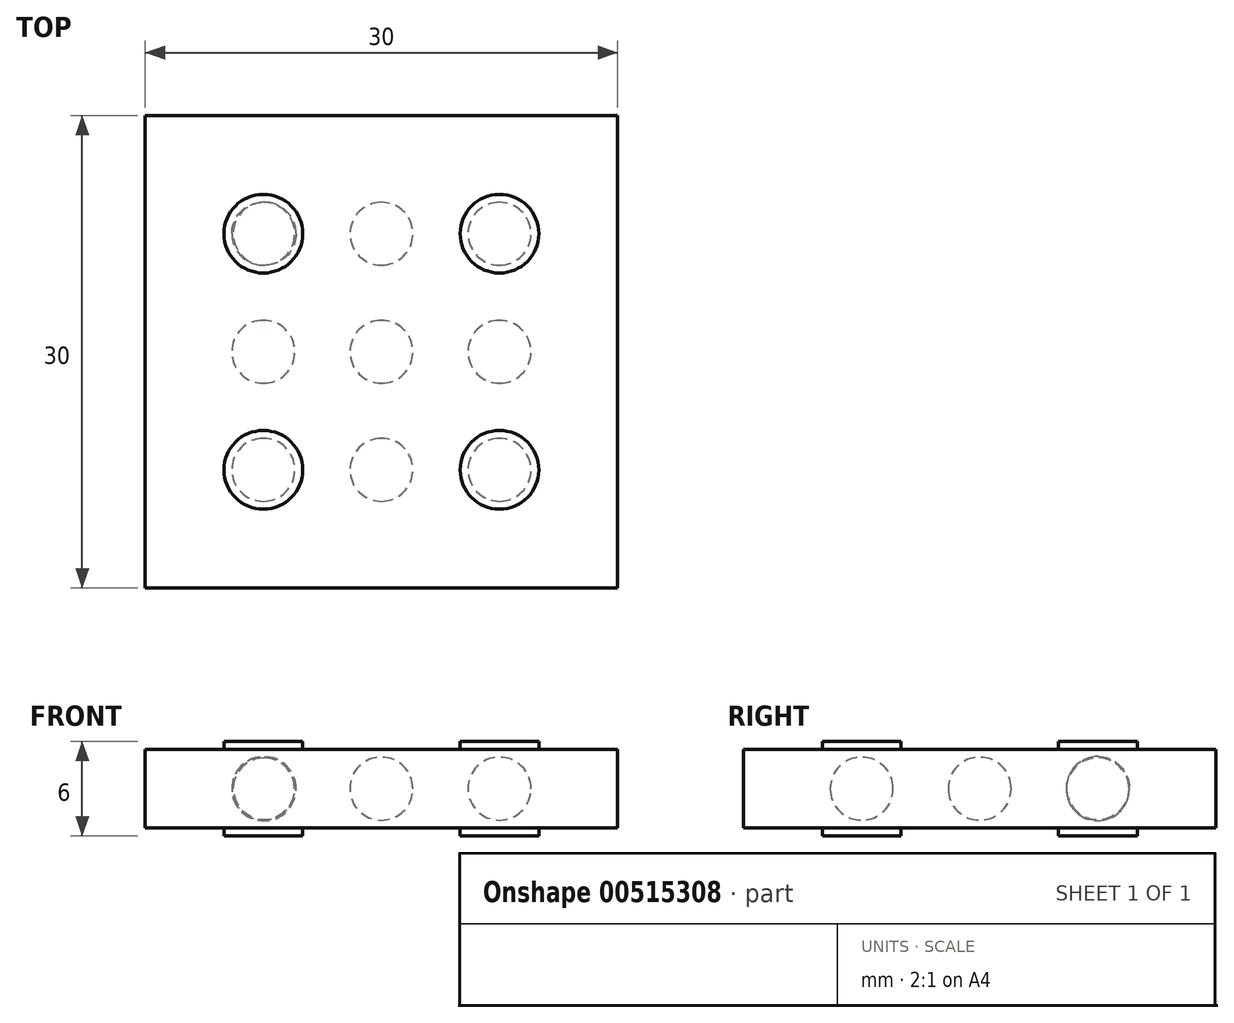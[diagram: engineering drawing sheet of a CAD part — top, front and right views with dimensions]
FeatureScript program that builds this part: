
annotation { "Feature Type Name" : "Feature", "Feature Type Description" : "" }
export const myFeature = defineFeature(function(context is Context, id is Id, definition is map)
    precondition{}
    {
        {
            var Q0;
            Q0=qCreatedBy(makeId("Top.planeOp"),FACE);
            var sketch = newSketch(context, id + "F0", { "sketchPlane" : qUnion([Q0])});
            skCircle(sketch, "E0", {"center": v(-7.5, 7.5) * mm, "radius": 2.5 * mm});
            skCircle(sketch, "E1", {"center": v(7.5, 7.5) * mm, "radius": 2.5 * mm});
            skCircle(sketch, "E2", {"center": v(7.5, -7.5) * mm, "radius": 2.5 * mm});
            skCircle(sketch, "E3", {"center": v(-7.5, -7.5) * mm, "radius": 2.5 * mm});
            skSolve(sketch);
        }
        {
            var Q0;
            Q0 = qSketchRegion(id + "F0", true);
            extrude(context, id + "F1", {"entities" : qUnion([Q0]), "depth" : .5 * mm, "offsetDistance" : 25 * mm});
        }
        {
            var Q0;
            Q0=makeQuery(id+"F1.opExtrude","CAP_FACE",FACE,{"disambiguationData":[OSD([sQuery(id+"F0.wireOp",EDGE,"E0")])],"isStart":false});
            var sketch = newSketch(context, id + "F2", { "sketchPlane" : qUnion([Q0])});
            skLineSegment(sketch, "E4.bottom", {"start": v(-15, 15) * mm, "end": v(15, 15) * mm});
            skLineSegment(sketch, "E4.top", {"start": v(-15, -15) * mm, "end": v(15, -15) * mm});
            skLineSegment(sketch, "E4.left", {"start": v(-15, 15) * mm, "end": v(-15, -15) * mm});
            skLineSegment(sketch, "E4.right", {"start": v(15, 15) * mm, "end": v(15, -15) * mm});
            skSolve(sketch);
        }
        {
            var Q0;
            Q0 = qSketchRegion(id + "F2", true);
            extrude(context, id + "F3", {"entities" : qUnion([Q0]), "operationType" : NewBodyOperationType.ADD, "depth" : 5 * mm, "offsetDistance" : 25 * mm});
        }
        {
            var Q0;
            Q0=makeQuery(id+"F3.opExtrude","CAP_FACE",FACE,{"disambiguationData":[OSD([sQuery(id+"F2.wireOp",EDGE,"E4.bottom"),sQuery(id+"F2.wireOp",EDGE,"E4.top"),sQuery(id+"F2.wireOp",EDGE,"E4.left"),sQuery(id+"F2.wireOp",EDGE,"E4.right")])],"isStart":false});
            var sketch = newSketch(context, id + "F4", { "sketchPlane" : qUnion([Q0])});
            skCircle(sketch, "E5", {"center": v(7.5, 7.5) * mm, "radius": 2.5 * mm});
            skCircle(sketch, "E6", {"center": v(7.5, -7.5) * mm, "radius": 2.5 * mm});
            skCircle(sketch, "E7", {"center": v(-7.5, -7.5) * mm, "radius": 2.5 * mm});
            skCircle(sketch, "E8", {"center": v(-7.5, 7.5) * mm, "radius": 2.5 * mm});
            skSolve(sketch);
        }
        {
            var Q0;
            Q0 = qSketchRegion(id + "F4", true);
            extrude(context, id + "F5", {"entities" : qUnion([Q0]), "operationType" : NewBodyOperationType.ADD, "depth" : .5 * mm, "offsetDistance" : 25 * mm});
        }
        {
            var Q0;
            Q0=qCreatedBy(makeId("Top.planeOp"),FACE);
            cPlane(context, id + "F6", {"entities" : qUnion([Q0]), "cplaneType" : CPlaneType.OFFSET, "offset" : 3 * mm, "width" : 150 * mm, "height" : 150 * mm});
        }
        {
            var Q0;
            Q0=qCreatedBy(id+"F6.planeOp",FACE);
            var sketch = newSketch(context, id + "F7", { "sketchPlane" : qUnion([Q0])});
            skLineSegment(sketch, "E9", {"start": v(-7.46, 9.5) * mm, "end": v(-7.46, 5.5) * mm});
            skArc(sketch, "E10", {"start": v(-7.46, 5.5) * mm, "mid": v(-5.5, 7.5) * mm, "end": v(-7.46, 9.5) * mm});
            skSolve(sketch);
        }
        {
            var Q0;
            Q0 = qSketchRegion(id + "F7", true);
            var Q1;
            Q1=sQuery(id+"F7.wireOp",EDGE,"E9");
            revolve(context, id + "F8", {"operationType" : NewBodyOperationType.REMOVE, "entities" : qUnion([Q0]), "axis" : qUnion([Q1]), "revolveType" : RevolveType.FULL, "oppositeDirection" : true});
        }
        {
            var Q0;
            Q0=qCreatedBy(id+"F6.planeOp",FACE);
            var sketch = newSketch(context, id + "F9", { "sketchPlane" : qUnion([Q0])});
            skLineSegment(sketch, "E11", {"start": v(0, 9.5) * mm, "end": v(0, 5.5) * mm});
            skArc(sketch, "E12", {"start": v(0, 5.5) * mm, "mid": v(2, 7.5) * mm, "end": v(0, 9.5) * mm});
            skSolve(sketch);
        }
        {
            var Q0;
            Q0 = qSketchRegion(id + "F9", true);
            var Q1;
            Q1=sQuery(id+"F9.wireOp",EDGE,"E11");
            revolve(context, id + "F10", {"operationType" : NewBodyOperationType.REMOVE, "entities" : qUnion([Q0]), "axis" : qUnion([Q1]), "revolveType" : RevolveType.FULL, "oppositeDirection" : true});
        }
        {
            var Q0;
            Q0=qCreatedBy(id+"F6.planeOp",FACE);
            var sketch = newSketch(context, id + "F11", { "sketchPlane" : qUnion([Q0])});
            skLineSegment(sketch, "E13", {"start": v(7.5, 9.5) * mm, "end": v(7.5, 5.5) * mm});
            skArc(sketch, "E14", {"start": v(7.5, 5.5) * mm, "mid": v(9.5, 7.5) * mm, "end": v(7.5, 9.5) * mm});
            skSolve(sketch);
        }
        {
            var Q0;
            Q0 = qSketchRegion(id + "F11", true);
            var Q1;
            Q1=sQuery(id+"F11.wireOp",EDGE,"E13");
            revolve(context, id + "F12", {"operationType" : NewBodyOperationType.REMOVE, "entities" : qUnion([Q0]), "axis" : qUnion([Q1]), "revolveType" : RevolveType.FULL, "oppositeDirection" : true});
        }
        {
            var Q0;
            Q0=qCreatedBy(id+"F6.planeOp",FACE);
            var sketch = newSketch(context, id + "F13", { "sketchPlane" : qUnion([Q0])});
            skLineSegment(sketch, "E15", {"start": v(-7.5, 2) * mm, "end": v(-7.5, -2) * mm});
            skArc(sketch, "E16", {"start": v(-7.5, -2) * mm, "mid": v(-5.5, 0) * mm, "end": v(-7.5, 2) * mm});
            skSolve(sketch);
        }
        {
            var Q0;
            Q0 = qSketchRegion(id + "F13", true);
            var Q1;
            Q1=sQuery(id+"F13.wireOp",EDGE,"E15");
            revolve(context, id + "F14", {"operationType" : NewBodyOperationType.REMOVE, "entities" : qUnion([Q0]), "axis" : qUnion([Q1]), "revolveType" : RevolveType.FULL, "oppositeDirection" : true});
        }
        {
            var Q0;
            Q0=qCreatedBy(id+"F6.planeOp",FACE);
            var sketch = newSketch(context, id + "F15", { "sketchPlane" : qUnion([Q0])});
            skLineSegment(sketch, "E17", {"start": v(0, 2) * mm, "end": v(0, -2) * mm});
            skArc(sketch, "E18", {"start": v(0, -2) * mm, "mid": v(2, 0) * mm, "end": v(0, 2) * mm});
            skSolve(sketch);
        }
        {
            var Q0;
            Q0 = qSketchRegion(id + "F15", true);
            var Q1;
            Q1=sQuery(id+"F15.wireOp",EDGE,"E17");
            revolve(context, id + "F16", {"operationType" : NewBodyOperationType.REMOVE, "entities" : qUnion([Q0]), "axis" : qUnion([Q1]), "revolveType" : RevolveType.FULL, "oppositeDirection" : true});
        }
        {
            var Q0;
            Q0=qCreatedBy(id+"F6.planeOp",FACE);
            var sketch = newSketch(context, id + "F17", { "sketchPlane" : qUnion([Q0])});
            skLineSegment(sketch, "E19", {"start": v(7.5, 2) * mm, "end": v(7.5, -2) * mm});
            skArc(sketch, "E20", {"start": v(7.5, -2) * mm, "mid": v(9.5, 0) * mm, "end": v(7.5, 2) * mm});
            skSolve(sketch);
        }
        {
            var Q0;
            Q0 = qSketchRegion(id + "F17", true);
            var Q1;
            Q1=sQuery(id+"F17.wireOp",EDGE,"E19");
            revolve(context, id + "F18", {"operationType" : NewBodyOperationType.REMOVE, "entities" : qUnion([Q0]), "axis" : qUnion([Q1]), "revolveType" : RevolveType.FULL});
        }
        {
            var Q0;
            Q0=qCreatedBy(id+"F6.planeOp",FACE);
            var sketch = newSketch(context, id + "F19", { "sketchPlane" : qUnion([Q0])});
            skLineSegment(sketch, "E21", {"start": v(-7.5, -5.5) * mm, "end": v(-7.5, -9.5) * mm});
            skArc(sketch, "E22", {"start": v(-7.5, -9.5) * mm, "mid": v(-5.5, -7.5) * mm, "end": v(-7.5, -5.5) * mm});
            skSolve(sketch);
        }
        {
            var Q0;
            Q0 = qSketchRegion(id + "F19", true);
            var Q1;
            Q1=sQuery(id+"F19.wireOp",EDGE,"E21");
            revolve(context, id + "F20", {"operationType" : NewBodyOperationType.REMOVE, "entities" : qUnion([Q0]), "axis" : qUnion([Q1]), "revolveType" : RevolveType.FULL, "oppositeDirection" : true});
        }
        {
            var Q0;
            Q0=qCreatedBy(id+"F6.planeOp",FACE);
            var sketch = newSketch(context, id + "F21", { "sketchPlane" : qUnion([Q0])});
            skLineSegment(sketch, "E23", {"start": v(0, -5.5) * mm, "end": v(0, -9.5) * mm});
            skArc(sketch, "E24", {"start": v(0, -9.5) * mm, "mid": v(2, -7.5) * mm, "end": v(0, -5.5) * mm});
            skSolve(sketch);
        }
        {
            var Q0;
            Q0 = qSketchRegion(id + "F21", true);
            var Q1;
            Q1=sQuery(id+"F21.wireOp",EDGE,"E23");
            revolve(context, id + "F22", {"operationType" : NewBodyOperationType.REMOVE, "entities" : qUnion([Q0]), "axis" : qUnion([Q1]), "revolveType" : RevolveType.FULL, "oppositeDirection" : true});
        }
        {
            var Q0;
            Q0=qCreatedBy(id+"F6.planeOp",FACE);
            var sketch = newSketch(context, id + "F23", { "sketchPlane" : qUnion([Q0])});
            skLineSegment(sketch, "E25", {"start": v(7.5, -5.5) * mm, "end": v(7.5, -9.5) * mm});
            skArc(sketch, "E26", {"start": v(7.5, -9.5) * mm, "mid": v(9.5, -7.5) * mm, "end": v(7.5, -5.5) * mm});
            skSolve(sketch);
        }
        {
            var Q0;
            Q0 = qSketchRegion(id + "F23", true);
            var Q1;
            Q1=sQuery(id+"F23.wireOp",EDGE,"E25");
            revolve(context, id + "F24", {"operationType" : NewBodyOperationType.REMOVE, "entities" : qUnion([Q0]), "axis" : qUnion([Q1]), "revolveType" : RevolveType.FULL, "oppositeDirection" : true});
        }
    });
